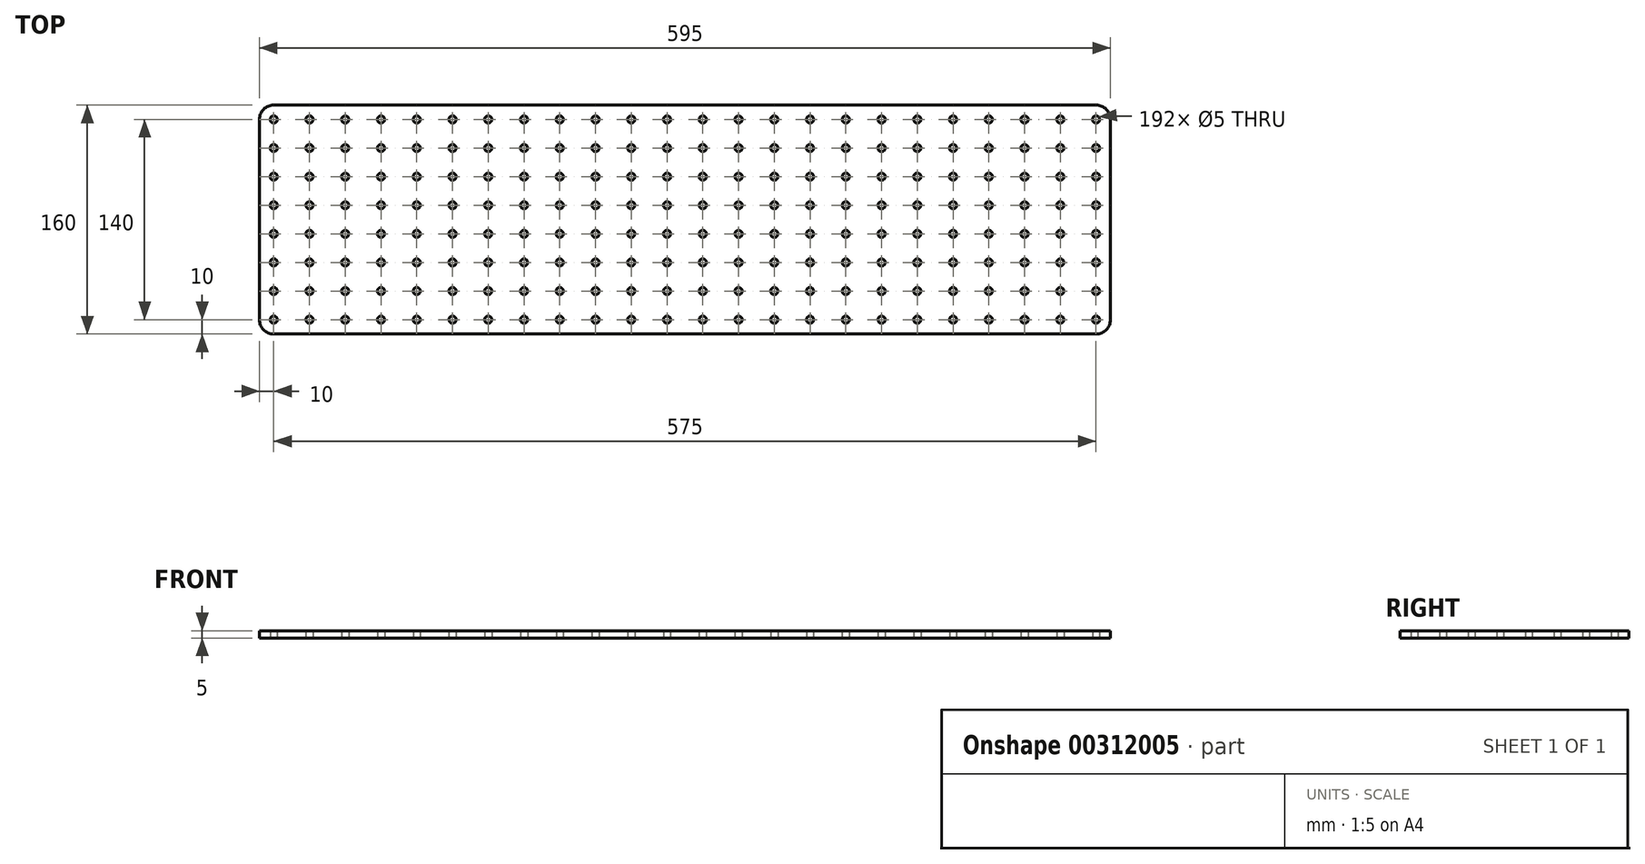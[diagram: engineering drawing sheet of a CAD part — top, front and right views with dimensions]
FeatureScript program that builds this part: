
annotation { "Feature Type Name" : "Feature", "Feature Type Description" : "" }
export const myFeature = defineFeature(function(context is Context, id is Id, definition is map)
    precondition{}
    {
        {
            var Q0;
            Q0=qCreatedBy(makeId("Top.planeOp"),FACE);
            var sketch = newSketch(context, id + "F0", { "sketchPlane" : qUnion([Q0])});
            skLineSegment(sketch, "E0.bottom", {"start": v(-287.5, 80) * mm, "end": v(287.5, 80) * mm});
            skLineSegment(sketch, "E0.top", {"start": v(-287.5, -80) * mm, "end": v(287.5, -80) * mm});
            skLineSegment(sketch, "E0.left", {"start": v(-297.5, 70) * mm, "end": v(-297.5, -70) * mm});
            skLineSegment(sketch, "E0.right", {"start": v(297.5, 70) * mm, "end": v(297.5, -70) * mm});
            skPoint(sketch, "E1", {"position": v(0, 80) * mm});
            skPoint(sketch, "E2", {"position": v(297.5, 0) * mm});
            skCircle(sketch, "E3", {"center": v(-287.5, 70) * mm, "radius": 2.5 * mm});
            skCircle(sketch, "E4.0.1.0", {"center": v(-287.5, 50) * mm, "radius": 2.5 * mm});
            skCircle(sketch, "E4.0.2.0", {"center": v(-287.5, 30) * mm, "radius": 2.5 * mm});
            skCircle(sketch, "E4.0.3.0", {"center": v(-287.5, 10) * mm, "radius": 2.5 * mm});
            skCircle(sketch, "E4.0.4.0", {"center": v(-287.5, -10) * mm, "radius": 2.5 * mm});
            skCircle(sketch, "E4.0.5.0", {"center": v(-287.5, -30) * mm, "radius": 2.5 * mm});
            skCircle(sketch, "E4.0.6.0", {"center": v(-287.5, -50) * mm, "radius": 2.5 * mm});
            skCircle(sketch, "E4.0.7.0", {"center": v(-287.5, -70) * mm, "radius": 2.5 * mm});
            skCircle(sketch, "E4.1.0.0", {"center": v(-262.5, 70) * mm, "radius": 2.5 * mm});
            skCircle(sketch, "E4.1.1.0", {"center": v(-262.5, 50) * mm, "radius": 2.5 * mm});
            skCircle(sketch, "E4.1.2.0", {"center": v(-262.5, 30) * mm, "radius": 2.5 * mm});
            skCircle(sketch, "E4.1.3.0", {"center": v(-262.5, 10) * mm, "radius": 2.5 * mm});
            skCircle(sketch, "E4.1.4.0", {"center": v(-262.5, -10) * mm, "radius": 2.5 * mm});
            skCircle(sketch, "E4.1.5.0", {"center": v(-262.5, -30) * mm, "radius": 2.5 * mm});
            skCircle(sketch, "E4.1.6.0", {"center": v(-262.5, -50) * mm, "radius": 2.5 * mm});
            skCircle(sketch, "E4.1.7.0", {"center": v(-262.5, -70) * mm, "radius": 2.5 * mm});
            skCircle(sketch, "E4.2.0.0", {"center": v(-237.5, 70) * mm, "radius": 2.5 * mm});
            skCircle(sketch, "E4.2.1.0", {"center": v(-237.5, 50) * mm, "radius": 2.5 * mm});
            skCircle(sketch, "E4.2.2.0", {"center": v(-237.5, 30) * mm, "radius": 2.5 * mm});
            skCircle(sketch, "E4.2.3.0", {"center": v(-237.5, 10) * mm, "radius": 2.5 * mm});
            skCircle(sketch, "E4.2.4.0", {"center": v(-237.5, -10) * mm, "radius": 2.5 * mm});
            skCircle(sketch, "E4.2.5.0", {"center": v(-237.5, -30) * mm, "radius": 2.5 * mm});
            skCircle(sketch, "E4.2.6.0", {"center": v(-237.5, -50) * mm, "radius": 2.5 * mm});
            skCircle(sketch, "E4.2.7.0", {"center": v(-237.5, -70) * mm, "radius": 2.5 * mm});
            skCircle(sketch, "E4.3.0.0", {"center": v(-212.5, 70) * mm, "radius": 2.5 * mm});
            skCircle(sketch, "E4.3.1.0", {"center": v(-212.5, 50) * mm, "radius": 2.5 * mm});
            skCircle(sketch, "E4.3.2.0", {"center": v(-212.5, 30) * mm, "radius": 2.5 * mm});
            skCircle(sketch, "E4.3.3.0", {"center": v(-212.5, 10) * mm, "radius": 2.5 * mm});
            skCircle(sketch, "E4.3.4.0", {"center": v(-212.5, -10) * mm, "radius": 2.5 * mm});
            skCircle(sketch, "E4.3.5.0", {"center": v(-212.5, -30) * mm, "radius": 2.5 * mm});
            skCircle(sketch, "E4.3.6.0", {"center": v(-212.5, -50) * mm, "radius": 2.5 * mm});
            skCircle(sketch, "E4.3.7.0", {"center": v(-212.5, -70) * mm, "radius": 2.5 * mm});
            skCircle(sketch, "E4.4.0.0", {"center": v(-187.5, 70) * mm, "radius": 2.5 * mm});
            skCircle(sketch, "E4.4.1.0", {"center": v(-187.5, 50) * mm, "radius": 2.5 * mm});
            skCircle(sketch, "E4.4.2.0", {"center": v(-187.5, 30) * mm, "radius": 2.5 * mm});
            skCircle(sketch, "E4.4.3.0", {"center": v(-187.5, 10) * mm, "radius": 2.5 * mm});
            skCircle(sketch, "E4.4.4.0", {"center": v(-187.5, -10) * mm, "radius": 2.5 * mm});
            skCircle(sketch, "E4.4.5.0", {"center": v(-187.5, -30) * mm, "radius": 2.5 * mm});
            skCircle(sketch, "E4.4.6.0", {"center": v(-187.5, -50) * mm, "radius": 2.5 * mm});
            skCircle(sketch, "E4.4.7.0", {"center": v(-187.5, -70) * mm, "radius": 2.5 * mm});
            skCircle(sketch, "E4.5.0.0", {"center": v(-162.5, 70) * mm, "radius": 2.5 * mm});
            skCircle(sketch, "E4.5.1.0", {"center": v(-162.5, 50) * mm, "radius": 2.5 * mm});
            skCircle(sketch, "E4.5.2.0", {"center": v(-162.5, 30) * mm, "radius": 2.5 * mm});
            skCircle(sketch, "E4.5.3.0", {"center": v(-162.5, 10) * mm, "radius": 2.5 * mm});
            skCircle(sketch, "E4.5.4.0", {"center": v(-162.5, -10) * mm, "radius": 2.5 * mm});
            skCircle(sketch, "E4.5.5.0", {"center": v(-162.5, -30) * mm, "radius": 2.5 * mm});
            skCircle(sketch, "E4.5.6.0", {"center": v(-162.5, -50) * mm, "radius": 2.5 * mm});
            skCircle(sketch, "E4.5.7.0", {"center": v(-162.5, -70) * mm, "radius": 2.5 * mm});
            skCircle(sketch, "E4.6.0.0", {"center": v(-137.5, 70) * mm, "radius": 2.5 * mm});
            skCircle(sketch, "E4.6.1.0", {"center": v(-137.5, 50) * mm, "radius": 2.5 * mm});
            skCircle(sketch, "E4.6.2.0", {"center": v(-137.5, 30) * mm, "radius": 2.5 * mm});
            skCircle(sketch, "E4.6.3.0", {"center": v(-137.5, 10) * mm, "radius": 2.5 * mm});
            skCircle(sketch, "E4.6.4.0", {"center": v(-137.5, -10) * mm, "radius": 2.5 * mm});
            skCircle(sketch, "E4.6.5.0", {"center": v(-137.5, -30) * mm, "radius": 2.5 * mm});
            skCircle(sketch, "E4.6.6.0", {"center": v(-137.5, -50) * mm, "radius": 2.5 * mm});
            skCircle(sketch, "E4.6.7.0", {"center": v(-137.5, -70) * mm, "radius": 2.5 * mm});
            skCircle(sketch, "E4.7.0.0", {"center": v(-112.5, 70) * mm, "radius": 2.5 * mm});
            skCircle(sketch, "E4.7.1.0", {"center": v(-112.5, 50) * mm, "radius": 2.5 * mm});
            skCircle(sketch, "E4.7.2.0", {"center": v(-112.5, 30) * mm, "radius": 2.5 * mm});
            skCircle(sketch, "E4.7.3.0", {"center": v(-112.5, 10) * mm, "radius": 2.5 * mm});
            skCircle(sketch, "E4.7.4.0", {"center": v(-112.5, -10) * mm, "radius": 2.5 * mm});
            skCircle(sketch, "E4.7.5.0", {"center": v(-112.5, -30) * mm, "radius": 2.5 * mm});
            skCircle(sketch, "E4.7.6.0", {"center": v(-112.5, -50) * mm, "radius": 2.5 * mm});
            skCircle(sketch, "E4.7.7.0", {"center": v(-112.5, -70) * mm, "radius": 2.5 * mm});
            skCircle(sketch, "E4.8.0.0", {"center": v(-87.5, 70) * mm, "radius": 2.5 * mm});
            skCircle(sketch, "E4.8.1.0", {"center": v(-87.5, 50) * mm, "radius": 2.5 * mm});
            skCircle(sketch, "E4.8.2.0", {"center": v(-87.5, 30) * mm, "radius": 2.5 * mm});
            skCircle(sketch, "E4.8.3.0", {"center": v(-87.5, 10) * mm, "radius": 2.5 * mm});
            skCircle(sketch, "E4.8.4.0", {"center": v(-87.5, -10) * mm, "radius": 2.5 * mm});
            skCircle(sketch, "E4.8.5.0", {"center": v(-87.5, -30) * mm, "radius": 2.5 * mm});
            skCircle(sketch, "E4.8.6.0", {"center": v(-87.5, -50) * mm, "radius": 2.5 * mm});
            skCircle(sketch, "E4.8.7.0", {"center": v(-87.5, -70) * mm, "radius": 2.5 * mm});
            skCircle(sketch, "E4.9.0.0", {"center": v(-62.5, 70) * mm, "radius": 2.5 * mm});
            skCircle(sketch, "E4.9.1.0", {"center": v(-62.5, 50) * mm, "radius": 2.5 * mm});
            skCircle(sketch, "E4.9.2.0", {"center": v(-62.5, 30) * mm, "radius": 2.5 * mm});
            skCircle(sketch, "E4.9.3.0", {"center": v(-62.5, 10) * mm, "radius": 2.5 * mm});
            skCircle(sketch, "E4.9.4.0", {"center": v(-62.5, -10) * mm, "radius": 2.5 * mm});
            skCircle(sketch, "E4.9.5.0", {"center": v(-62.5, -30) * mm, "radius": 2.5 * mm});
            skCircle(sketch, "E4.9.6.0", {"center": v(-62.5, -50) * mm, "radius": 2.5 * mm});
            skCircle(sketch, "E4.9.7.0", {"center": v(-62.5, -70) * mm, "radius": 2.5 * mm});
            skCircle(sketch, "E4.10.0.0", {"center": v(-37.5, 70) * mm, "radius": 2.5 * mm});
            skCircle(sketch, "E4.10.1.0", {"center": v(-37.5, 50) * mm, "radius": 2.5 * mm});
            skCircle(sketch, "E4.10.2.0", {"center": v(-37.5, 30) * mm, "radius": 2.5 * mm});
            skCircle(sketch, "E4.10.3.0", {"center": v(-37.5, 10) * mm, "radius": 2.5 * mm});
            skCircle(sketch, "E4.10.4.0", {"center": v(-37.5, -10) * mm, "radius": 2.5 * mm});
            skCircle(sketch, "E4.10.5.0", {"center": v(-37.5, -30) * mm, "radius": 2.5 * mm});
            skCircle(sketch, "E4.10.6.0", {"center": v(-37.5, -50) * mm, "radius": 2.5 * mm});
            skCircle(sketch, "E4.10.7.0", {"center": v(-37.5, -70) * mm, "radius": 2.5 * mm});
            skCircle(sketch, "E4.11.0.0", {"center": v(-12.5, 70) * mm, "radius": 2.5 * mm});
            skCircle(sketch, "E4.11.1.0", {"center": v(-12.5, 50) * mm, "radius": 2.5 * mm});
            skCircle(sketch, "E4.11.2.0", {"center": v(-12.5, 30) * mm, "radius": 2.5 * mm});
            skCircle(sketch, "E4.11.3.0", {"center": v(-12.5, 10) * mm, "radius": 2.5 * mm});
            skCircle(sketch, "E4.11.4.0", {"center": v(-12.5, -10) * mm, "radius": 2.5 * mm});
            skCircle(sketch, "E4.11.5.0", {"center": v(-12.5, -30) * mm, "radius": 2.5 * mm});
            skCircle(sketch, "E4.11.6.0", {"center": v(-12.5, -50) * mm, "radius": 2.5 * mm});
            skCircle(sketch, "E4.11.7.0", {"center": v(-12.5, -70) * mm, "radius": 2.5 * mm});
            skCircle(sketch, "E4.12.0.0", {"center": v(12.5, 70) * mm, "radius": 2.5 * mm});
            skCircle(sketch, "E4.12.1.0", {"center": v(12.5, 50) * mm, "radius": 2.5 * mm});
            skCircle(sketch, "E4.12.2.0", {"center": v(12.5, 30) * mm, "radius": 2.5 * mm});
            skCircle(sketch, "E4.12.3.0", {"center": v(12.5, 10) * mm, "radius": 2.5 * mm});
            skCircle(sketch, "E4.12.4.0", {"center": v(12.5, -10) * mm, "radius": 2.5 * mm});
            skCircle(sketch, "E4.12.5.0", {"center": v(12.5, -30) * mm, "radius": 2.5 * mm});
            skCircle(sketch, "E4.12.6.0", {"center": v(12.5, -50) * mm, "radius": 2.5 * mm});
            skCircle(sketch, "E4.12.7.0", {"center": v(12.5, -70) * mm, "radius": 2.5 * mm});
            skCircle(sketch, "E4.13.0.0", {"center": v(37.5, 70) * mm, "radius": 2.5 * mm});
            skCircle(sketch, "E4.13.1.0", {"center": v(37.5, 50) * mm, "radius": 2.5 * mm});
            skCircle(sketch, "E4.13.2.0", {"center": v(37.5, 30) * mm, "radius": 2.5 * mm});
            skCircle(sketch, "E4.13.3.0", {"center": v(37.5, 10) * mm, "radius": 2.5 * mm});
            skCircle(sketch, "E4.13.4.0", {"center": v(37.5, -10) * mm, "radius": 2.5 * mm});
            skCircle(sketch, "E4.13.5.0", {"center": v(37.5, -30) * mm, "radius": 2.5 * mm});
            skCircle(sketch, "E4.13.6.0", {"center": v(37.5, -50) * mm, "radius": 2.5 * mm});
            skCircle(sketch, "E4.13.7.0", {"center": v(37.5, -70) * mm, "radius": 2.5 * mm});
            skCircle(sketch, "E4.14.0.0", {"center": v(62.5, 70) * mm, "radius": 2.5 * mm});
            skCircle(sketch, "E4.14.1.0", {"center": v(62.5, 50) * mm, "radius": 2.5 * mm});
            skCircle(sketch, "E4.14.2.0", {"center": v(62.5, 30) * mm, "radius": 2.5 * mm});
            skCircle(sketch, "E4.14.3.0", {"center": v(62.5, 10) * mm, "radius": 2.5 * mm});
            skCircle(sketch, "E4.14.4.0", {"center": v(62.5, -10) * mm, "radius": 2.5 * mm});
            skCircle(sketch, "E4.14.5.0", {"center": v(62.5, -30) * mm, "radius": 2.5 * mm});
            skCircle(sketch, "E4.14.6.0", {"center": v(62.5, -50) * mm, "radius": 2.5 * mm});
            skCircle(sketch, "E4.14.7.0", {"center": v(62.5, -70) * mm, "radius": 2.5 * mm});
            skCircle(sketch, "E4.15.0.0", {"center": v(87.5, 70) * mm, "radius": 2.5 * mm});
            skCircle(sketch, "E4.15.1.0", {"center": v(87.5, 50) * mm, "radius": 2.5 * mm});
            skCircle(sketch, "E4.15.2.0", {"center": v(87.5, 30) * mm, "radius": 2.5 * mm});
            skCircle(sketch, "E4.15.3.0", {"center": v(87.5, 10) * mm, "radius": 2.5 * mm});
            skCircle(sketch, "E4.15.4.0", {"center": v(87.5, -10) * mm, "radius": 2.5 * mm});
            skCircle(sketch, "E4.15.5.0", {"center": v(87.5, -30) * mm, "radius": 2.5 * mm});
            skCircle(sketch, "E4.15.6.0", {"center": v(87.5, -50) * mm, "radius": 2.5 * mm});
            skCircle(sketch, "E4.15.7.0", {"center": v(87.5, -70) * mm, "radius": 2.5 * mm});
            skCircle(sketch, "E4.16.0.0", {"center": v(112.5, 70) * mm, "radius": 2.5 * mm});
            skCircle(sketch, "E4.16.1.0", {"center": v(112.5, 50) * mm, "radius": 2.5 * mm});
            skCircle(sketch, "E4.16.2.0", {"center": v(112.5, 30) * mm, "radius": 2.5 * mm});
            skCircle(sketch, "E4.16.3.0", {"center": v(112.5, 10) * mm, "radius": 2.5 * mm});
            skCircle(sketch, "E4.16.4.0", {"center": v(112.5, -10) * mm, "radius": 2.5 * mm});
            skCircle(sketch, "E4.16.5.0", {"center": v(112.5, -30) * mm, "radius": 2.5 * mm});
            skCircle(sketch, "E4.16.6.0", {"center": v(112.5, -50) * mm, "radius": 2.5 * mm});
            skCircle(sketch, "E4.16.7.0", {"center": v(112.5, -70) * mm, "radius": 2.5 * mm});
            skCircle(sketch, "E4.17.0.0", {"center": v(137.5, 70) * mm, "radius": 2.5 * mm});
            skCircle(sketch, "E4.17.1.0", {"center": v(137.5, 50) * mm, "radius": 2.5 * mm});
            skCircle(sketch, "E4.17.2.0", {"center": v(137.5, 30) * mm, "radius": 2.5 * mm});
            skCircle(sketch, "E4.17.3.0", {"center": v(137.5, 10) * mm, "radius": 2.5 * mm});
            skCircle(sketch, "E4.17.4.0", {"center": v(137.5, -10) * mm, "radius": 2.5 * mm});
            skCircle(sketch, "E4.17.5.0", {"center": v(137.5, -30) * mm, "radius": 2.5 * mm});
            skCircle(sketch, "E4.17.6.0", {"center": v(137.5, -50) * mm, "radius": 2.5 * mm});
            skCircle(sketch, "E4.17.7.0", {"center": v(137.5, -70) * mm, "radius": 2.5 * mm});
            skCircle(sketch, "E4.18.0.0", {"center": v(162.5, 70) * mm, "radius": 2.5 * mm});
            skCircle(sketch, "E4.18.1.0", {"center": v(162.5, 50) * mm, "radius": 2.5 * mm});
            skCircle(sketch, "E4.18.2.0", {"center": v(162.5, 30) * mm, "radius": 2.5 * mm});
            skCircle(sketch, "E4.18.3.0", {"center": v(162.5, 10) * mm, "radius": 2.5 * mm});
            skCircle(sketch, "E4.18.4.0", {"center": v(162.5, -10) * mm, "radius": 2.5 * mm});
            skCircle(sketch, "E4.18.5.0", {"center": v(162.5, -30) * mm, "radius": 2.5 * mm});
            skCircle(sketch, "E4.18.6.0", {"center": v(162.5, -50) * mm, "radius": 2.5 * mm});
            skCircle(sketch, "E4.18.7.0", {"center": v(162.5, -70) * mm, "radius": 2.5 * mm});
            skCircle(sketch, "E4.19.0.0", {"center": v(187.5, 70) * mm, "radius": 2.5 * mm});
            skCircle(sketch, "E4.19.1.0", {"center": v(187.5, 50) * mm, "radius": 2.5 * mm});
            skCircle(sketch, "E4.19.2.0", {"center": v(187.5, 30) * mm, "radius": 2.5 * mm});
            skCircle(sketch, "E4.19.3.0", {"center": v(187.5, 10) * mm, "radius": 2.5 * mm});
            skCircle(sketch, "E4.19.4.0", {"center": v(187.5, -10) * mm, "radius": 2.5 * mm});
            skCircle(sketch, "E4.19.5.0", {"center": v(187.5, -30) * mm, "radius": 2.5 * mm});
            skCircle(sketch, "E4.19.6.0", {"center": v(187.5, -50) * mm, "radius": 2.5 * mm});
            skCircle(sketch, "E4.19.7.0", {"center": v(187.5, -70) * mm, "radius": 2.5 * mm});
            skCircle(sketch, "E4.20.0.0", {"center": v(212.5, 70) * mm, "radius": 2.5 * mm});
            skCircle(sketch, "E4.20.1.0", {"center": v(212.5, 50) * mm, "radius": 2.5 * mm});
            skCircle(sketch, "E4.20.2.0", {"center": v(212.5, 30) * mm, "radius": 2.5 * mm});
            skCircle(sketch, "E4.20.3.0", {"center": v(212.5, 10) * mm, "radius": 2.5 * mm});
            skCircle(sketch, "E4.20.4.0", {"center": v(212.5, -10) * mm, "radius": 2.5 * mm});
            skCircle(sketch, "E4.20.5.0", {"center": v(212.5, -30) * mm, "radius": 2.5 * mm});
            skCircle(sketch, "E4.20.6.0", {"center": v(212.5, -50) * mm, "radius": 2.5 * mm});
            skCircle(sketch, "E4.20.7.0", {"center": v(212.5, -70) * mm, "radius": 2.5 * mm});
            skCircle(sketch, "E4.21.0.0", {"center": v(237.5, 70) * mm, "radius": 2.5 * mm});
            skCircle(sketch, "E4.21.1.0", {"center": v(237.5, 50) * mm, "radius": 2.5 * mm});
            skCircle(sketch, "E4.21.2.0", {"center": v(237.5, 30) * mm, "radius": 2.5 * mm});
            skCircle(sketch, "E4.21.3.0", {"center": v(237.5, 10) * mm, "radius": 2.5 * mm});
            skCircle(sketch, "E4.21.4.0", {"center": v(237.5, -10) * mm, "radius": 2.5 * mm});
            skCircle(sketch, "E4.21.5.0", {"center": v(237.5, -30) * mm, "radius": 2.5 * mm});
            skCircle(sketch, "E4.21.6.0", {"center": v(237.5, -50) * mm, "radius": 2.5 * mm});
            skCircle(sketch, "E4.21.7.0", {"center": v(237.5, -70) * mm, "radius": 2.5 * mm});
            skCircle(sketch, "E4.22.0.0", {"center": v(262.5, 70) * mm, "radius": 2.5 * mm});
            skCircle(sketch, "E4.22.1.0", {"center": v(262.5, 50) * mm, "radius": 2.5 * mm});
            skCircle(sketch, "E4.22.2.0", {"center": v(262.5, 30) * mm, "radius": 2.5 * mm});
            skCircle(sketch, "E4.22.3.0", {"center": v(262.5, 10) * mm, "radius": 2.5 * mm});
            skCircle(sketch, "E4.22.4.0", {"center": v(262.5, -10) * mm, "radius": 2.5 * mm});
            skCircle(sketch, "E4.22.5.0", {"center": v(262.5, -30) * mm, "radius": 2.5 * mm});
            skCircle(sketch, "E4.22.6.0", {"center": v(262.5, -50) * mm, "radius": 2.5 * mm});
            skCircle(sketch, "E4.22.7.0", {"center": v(262.5, -70) * mm, "radius": 2.5 * mm});
            skCircle(sketch, "E4.23.0.0", {"center": v(287.5, 70) * mm, "radius": 2.5 * mm});
            skCircle(sketch, "E4.23.1.0", {"center": v(287.5, 50) * mm, "radius": 2.5 * mm});
            skCircle(sketch, "E4.23.2.0", {"center": v(287.5, 30) * mm, "radius": 2.5 * mm});
            skCircle(sketch, "E4.23.3.0", {"center": v(287.5, 10) * mm, "radius": 2.5 * mm});
            skCircle(sketch, "E4.23.4.0", {"center": v(287.5, -10) * mm, "radius": 2.5 * mm});
            skCircle(sketch, "E4.23.5.0", {"center": v(287.5, -30) * mm, "radius": 2.5 * mm});
            skCircle(sketch, "E4.23.6.0", {"center": v(287.5, -50) * mm, "radius": 2.5 * mm});
            skCircle(sketch, "E4.23.7.0", {"center": v(287.5, -70) * mm, "radius": 2.5 * mm});
            skLineSegment(sketch, "E4.direction1", {"start": v(-287.5, 70) * mm, "end": v(-262.5, 70) * mm, "construction": true});
            skLineSegment(sketch, "E4.direction2", {"start": v(-287.5, 70) * mm, "end": v(-287.5, 50) * mm, "construction": true});
            skArc(sketch, "E5", {"start": v(-297.5, 70) * mm, "mid": v(-294.57, 77.07) * mm, "end": v(-287.5, 80) * mm});
            skArc(sketch, "E6", {"start": v(-287.5, -80) * mm, "mid": v(-294.57, -77.07) * mm, "end": v(-297.5, -70) * mm});
            skArc(sketch, "E7", {"start": v(297.5, -70) * mm, "mid": v(294.57, -77.07) * mm, "end": v(287.5, -80) * mm});
            skArc(sketch, "E8", {"start": v(297.5, 70) * mm, "mid": v(294.57, 77.07) * mm, "end": v(287.5, 80) * mm});
            skPoint(sketch, "E9.orphan", {"position": v(-297.5, 80) * mm});
            skPoint(sketch, "E10.orphan", {"position": v(297.5, -80) * mm});
            skPoint(sketch, "E11.orphan", {"position": v(297.5, 80) * mm});
            skSolve(sketch);
        }
        {
            var Q0;
            Q0=makeQuery(id+"F0.imprint","IMPRINT",FACE,{"disambiguationData":[TD([[makeQuery(id+"F0.imprint","IMPRINT",EDGE,{"derivedFrom":sQuery(id+"F0.wireOp",EDGE,"E3")}),-1.0]])]});
            extrude(context, id + "F1", {"entities" : qUnion([Q0]), "depth" : 5 * mm});
        }
    });
